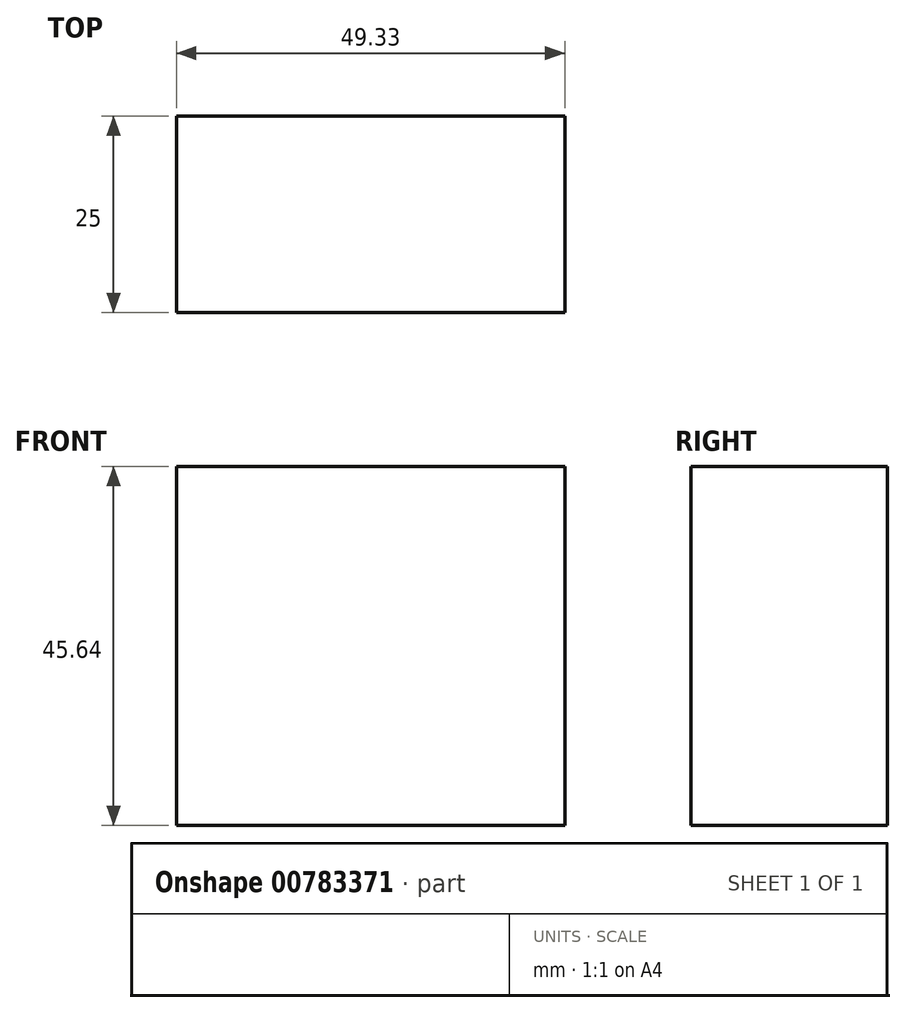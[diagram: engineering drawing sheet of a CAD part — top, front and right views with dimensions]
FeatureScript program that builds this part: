
annotation { "Feature Type Name" : "Feature", "Feature Type Description" : "" }
export const myFeature = defineFeature(function(context is Context, id is Id, definition is map)
    precondition{}
    {
        {
            var Q0;
            Q0=qCreatedBy(makeId("Front.planeOp"),FACE);
            var sketch = newSketch(context, id + "F0", { "sketchPlane" : qUnion([Q0])});
            skLineSegment(sketch, "E0.bottom", {"start": v(-125.32, 64.05) * mm, "end": v(-75.99, 64.05) * mm});
            skLineSegment(sketch, "E0.top", {"start": v(-125.32, 18.41) * mm, "end": v(-75.99, 18.41) * mm});
            skLineSegment(sketch, "E0.left", {"start": v(-125.32, 64.05) * mm, "end": v(-125.32, 18.41) * mm});
            skLineSegment(sketch, "E0.right", {"start": v(-75.99, 64.05) * mm, "end": v(-75.99, 18.41) * mm});
            skSolve(sketch);
        }
        {
            var Q0;
            Q0 = qSketchRegion(id + "F0", true);
            extrude(context, id + "F1", {"entities" : qUnion([Q0]), "depth" : 25 * mm, "offsetDistance" : 25 * mm});
        }
    });
